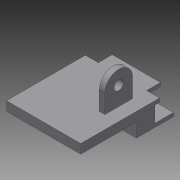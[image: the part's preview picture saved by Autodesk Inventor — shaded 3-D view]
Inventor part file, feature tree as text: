
AUTODESK INVENTOR PART (.ipt)
format: ipt  version: 2013 (Build 170138000, 138)  size: 161,792 bytes
history: native  units: mm
features: extrude x7, sketch x6, mirror x2, fillet x1
ambient origin geometry x8: Origin, YZ Plane, XZ Plane, XY Plane, X Axis, Y Axis, Z Axis, Center Point
bodies: Solid1 (feature_tree)
feature tree (16):
  extrude  "Extrusion1"  Depth=6.35mm
  extrude  "Extrusion2"  Depth=10.0mm
  extrude  "Extrusion3"  Depth=8.5mm TaperAngle=0.0deg
  mirror  "Mirror1"
  extrude  "Extrusion4"  Depth=2.0mm TaperAngle=0.0deg
  mirror  "Mirror2"
  extrude  "Extrusion5"  Depth=2.0mm TaperAngle=0.0deg
  extrude  "Extrusion6"  Depth=12.5mm
  extrude  "Extrusion7"  Depth=2.0mm TaperAngle=0.0deg
  fillet  "Fillet1"  Radius=5.0mm
  sketch  "Sketch1"  dims[d0=40.0mm d2=6.35mm]
  sketch  "Sketch2"  dims[d4=9.5mm d5=10.0mm]
  sketch  "Sketch4"  dims[d6=20.0mm d7=8.5mm d8=0.0mm]
  sketch  "Sketch5"  dims[d9=20.0mm d10=2.0mm d11=0.0mm]
  sketch  "Sketch6"  dims[d12=6.35mm d13=2.0mm d14=0.0mm]
  sketch  "Sketch7"  dims[d15=7.0mm d17=12.5mm d18=2.0mm d19=0.0mm d20=5.0mm d21=30.0mm d22=0.0mm d23=15.0mm d25=3.0mm d26=4.5mm d27=5.0mm d28=14.5mm d29=17.5mm d30=0.0mm d31=5.1mm d34=7.5mm d35=10.0mm d36=0.0mm d37=7.5mm]
